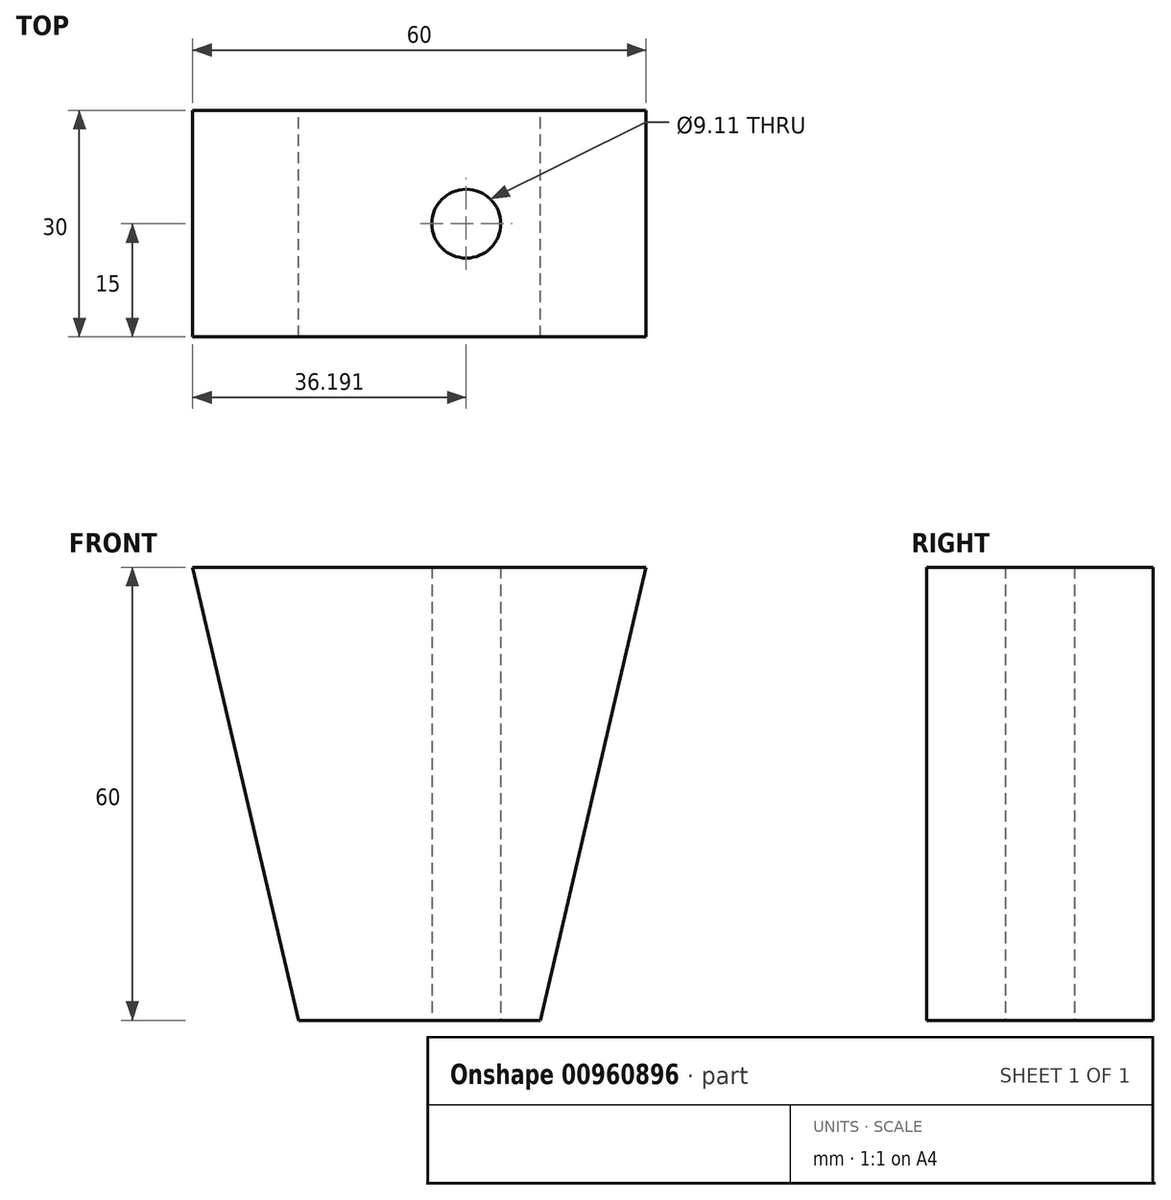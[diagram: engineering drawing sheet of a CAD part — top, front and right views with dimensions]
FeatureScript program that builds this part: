
annotation { "Feature Type Name" : "Feature", "Feature Type Description" : "" }
export const myFeature = defineFeature(function(context is Context, id is Id, definition is map)
    precondition{}
    {
        {
            var Q0;
            Q0=qCreatedBy(makeId("Front.planeOp"),FACE);
            var sketch = newSketch(context, id + "F0", { "sketchPlane" : qUnion([Q0])});
            skLineSegment(sketch, "E0", {"start": v(-30, 30) * mm, "end": v(-16, -30) * mm});
            skLineSegment(sketch, "E1", {"start": v(-16, -30) * mm, "end": v(16, -30) * mm});
            skLineSegment(sketch, "E2", {"start": v(16, -30) * mm, "end": v(30, 30) * mm});
            skLineSegment(sketch, "E3", {"start": v(30, 30) * mm, "end": v(-30, 30) * mm});
            skPoint(sketch, "E4", {"position": v(-7, -30) * mm});
            skPoint(sketch, "E5", {"position": v(7, -30) * mm});
            skPoint(sketch, "E6", {"position": v(20, 30) * mm});
            skPoint(sketch, "E7", {"position": v(-20, 30) * mm});
            skLineSegment(sketch, "E8", {"start": v(-20, 30) * mm, "end": v(-7, -30) * mm, "construction": true});
            skLineSegment(sketch, "E9", {"start": v(20, 30) * mm, "end": v(7, -30) * mm, "construction": true});
            skLineSegment(sketch, "E10", {"start": v(-25.12, 30) * mm, "end": v(-12.12, -30) * mm});
            skLineSegment(sketch, "E11", {"start": v(-12.12, -30) * mm, "end": v(-1.88, -30) * mm});
            skLineSegment(sketch, "E12", {"start": v(-1.88, -30) * mm, "end": v(-14.88, 30) * mm});
            skLineSegment(sketch, "E13", {"start": v(-25.12, 30) * mm, "end": v(-14.88, 30) * mm});
            skSolve(sketch);
        }
        {
            var Q0;
            {var subQ0=sQuery(id+"F0.wireOp",EDGE,"E2");Q0=makeQuery(id+"F0.imprint","IMPRINT",FACE,{"disambiguationData":[TD([[makeQuery(id+"F0.imprint","IMPRINT",EDGE,{"derivedFrom":subQ0}),1.0]])]});}
            var Q1;
            Q1=makeQuery(id+"F0.imprint","IMPRINT",FACE,{"disambiguationData":[TD([[makeQuery(id+"F0.imprint","IMPRINT",EDGE,{"derivedFrom":sQuery(id+"F0.wireOp",EDGE,"E10")}),1.0]])]});
            var Q2;
            {var subQ0=sQuery(id+"F0.wireOp",EDGE,"E0");Q2=makeQuery(id+"F0.imprint","IMPRINT",FACE,{"disambiguationData":[TD([[makeQuery(id+"F0.imprint","IMPRINT",EDGE,{"derivedFrom":subQ0}),1.0]])]});}
            extrude(context, id + "F1", {"entities" : qUnion([Q0, Q1, Q2]), "depth" : 15 * mm, "offsetDistance" : 25 * mm, "hasSecondDirection" : true, "secondDirectionOppositeDirection" : true, "secondDirectionDepth" : 15 * mm});
        }
        {
            var Q0;
            Q0=makeQuery(id+"F1.opExtrude","SWEPT_FACE",FACE,{"disambiguationData":[OSD([sQuery(id+"F0.wireOp",EDGE,"E1"),sQuery(id+"F0.wireOp",EDGE,"E11")])]});
            var sketch = newSketch(context, id + "F2", { "sketchPlane" : qUnion([Q0])});
            skCircle(sketch, "E14", {"center": v(6.2, 0) * mm, "radius": 4.55 * mm});
            skPoint(sketch, "E14.centerSnap0", {"position": v(16, 0) * mm});
            skSolve(sketch);
        }
        {
            var Q0;
            Q0=makeQuery(id+"F2.imprint","IMPRINT",FACE,{"disambiguationData":[TD([[makeQuery(id+"F2.imprint","IMPRINT",EDGE,{"derivedFrom":sQuery(id+"F2.wireOp",EDGE,"E14")}),1.0]])]});
            var Q1;
            Q1=sQuery(id+"F2.wireOp",EDGE,"E14");
            extrude(context, id + "F3", {"entities" : qUnion([Q0]), "operationType" : NewBodyOperationType.REMOVE, "surfaceEntities" : qUnion([Q1]), "oppositeDirection" : true, "depth" : 65.6 * mm, "offsetDistance" : 25 * mm});
        }
    });
